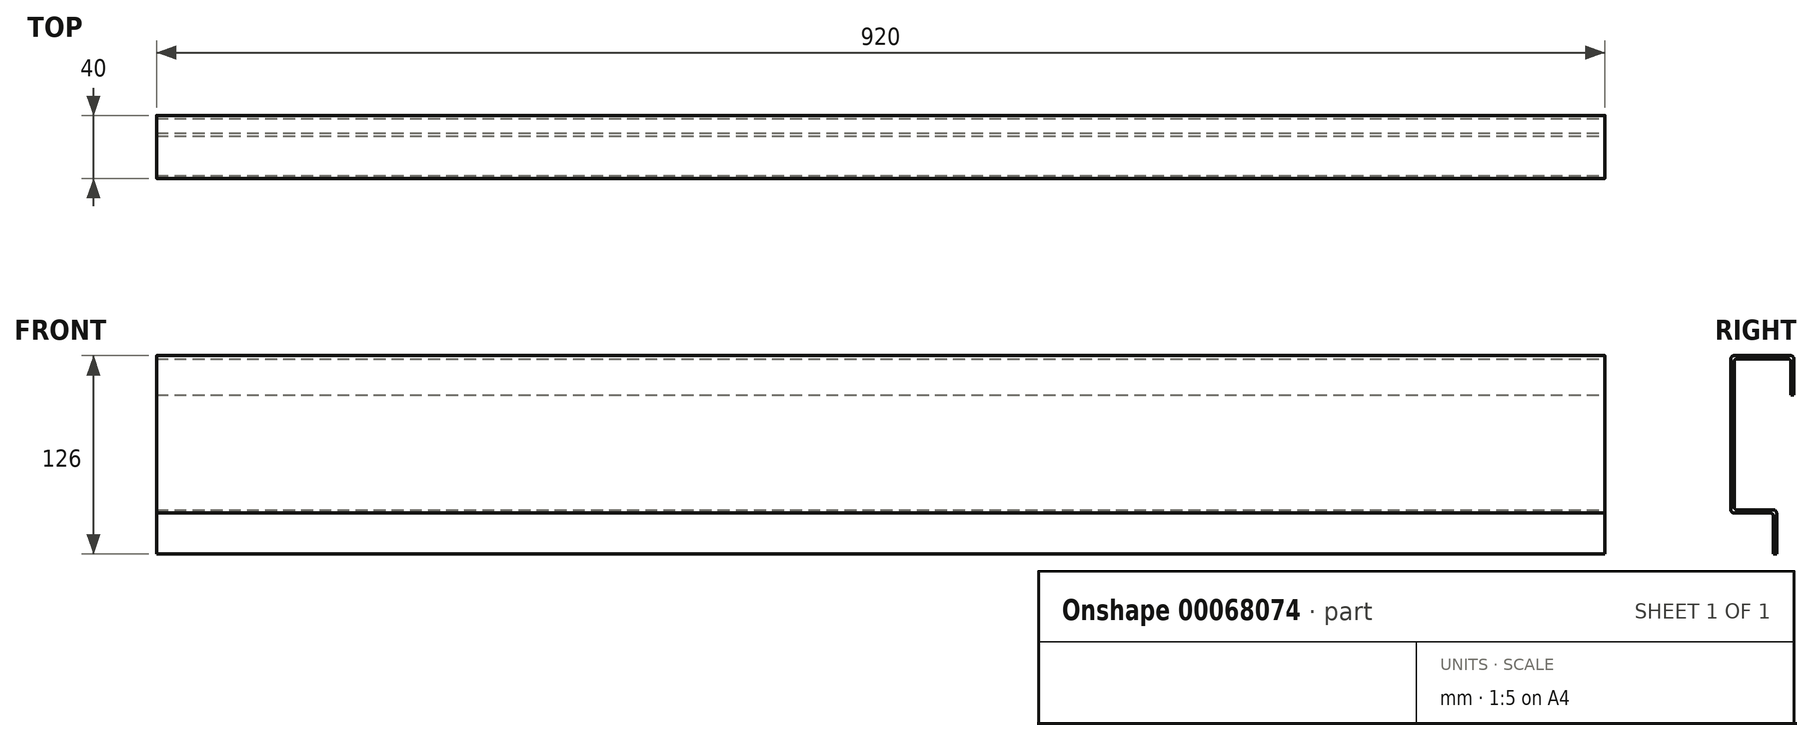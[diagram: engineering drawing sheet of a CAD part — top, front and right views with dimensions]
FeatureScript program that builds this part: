
annotation { "Feature Type Name" : "Feature", "Feature Type Description" : "" }
export const myFeature = defineFeature(function(context is Context, id is Id, definition is map)
    precondition{}
    {
        {
            var Q0;
            Q0=qCreatedBy(makeId("Right.planeOp"),FACE);
            var sketch = newSketch(context, id + "F0", { "sketchPlane" : qUnion([Q0])});
            skLineSegment(sketch, "E0", {"start": v(38, -25) * mm, "end": v(38, -2) * mm});
            skLineSegment(sketch, "E1", {"start": v(38, -2) * mm, "end": v(2, -2) * mm});
            skLineSegment(sketch, "E2", {"start": v(2, -2) * mm, "end": v(2, -98) * mm});
            skLineSegment(sketch, "E3", {"start": v(2, -98) * mm, "end": v(29, -98) * mm});
            skLineSegment(sketch, "E4.0", {"start": v(0, -100) * mm, "end": v(27, -100) * mm});
            skLineSegment(sketch, "E4.1", {"start": v(0, 0) * mm, "end": v(0, -100) * mm});
            skLineSegment(sketch, "E4.2", {"start": v(40, 0) * mm, "end": v(0, 0) * mm});
            skLineSegment(sketch, "E4.3", {"start": v(40, -25) * mm, "end": v(40, 0) * mm});
            skLineSegment(sketch, "E5", {"start": v(29, -98) * mm, "end": v(29, -126) * mm});
            skLineSegment(sketch, "E6", {"start": v(27, -100) * mm, "end": v(27, -126) * mm});
            skLineSegment(sketch, "E7", {"start": v(40, -25) * mm, "end": v(38, -25) * mm});
            skLineSegment(sketch, "E8", {"start": v(29, -126) * mm, "end": v(27, -126) * mm});
            skSolve(sketch);
        }
        {
            var Q0;
            Q0=qCreatedBy(makeId("Top.planeOp"),FACE);
            var sketch = newSketch(context, id + "F1", { "sketchPlane" : qUnion([Q0])});
            skLineSegment(sketch, "E9", {"start": v(0, 0) * mm, "end": v(920, 0) * mm});
            skSolve(sketch);
        }
        {
            var Q0;
            Q0 = qSketchRegion(id + "F0", true);
            var Q1;
            Q1 = qConstructionFilter(qBodyType(qCreatedBy(id + "F1" ,EDGE), BodyType.WIRE), ConstructionObject.NO);
            sweep(context, id + "F2", {"profiles" : qUnion([Q0]), "path" : qUnion([Q1])});
        }
        {
            var Q0;
            Q0=makeQuery(id+"F2.opSweep","SWEPT_EDGE",EDGE,{"disambiguationData":[OSD([sQuery(id+"F0.wireOp",EDGE,"E4.2"),sQuery(id+"F0.wireOp",EDGE,"E4.3"),sQuery(id+"F1.wireOp",EDGE,"E9")])]});
            var Q1;
            Q1=makeQuery(id+"F2.opSweep","SWEPT_EDGE",EDGE,{"disambiguationData":[OSD([sQuery(id+"F0.wireOp",EDGE,"E4.1"),sQuery(id+"F0.wireOp",EDGE,"E4.2"),sQuery(id+"F1.wireOp",EDGE,"E9")])]});
            var Q2;
            Q2=makeQuery(id+"F2.opSweep","SWEPT_EDGE",EDGE,{"disambiguationData":[OSD([sQuery(id+"F0.wireOp",EDGE,"E3"),sQuery(id+"F0.wireOp",EDGE,"E5"),sQuery(id+"F1.wireOp",EDGE,"E9")])]});
            var Q3;
            Q3=makeQuery(id+"F2.opSweep","SWEPT_EDGE",EDGE,{"disambiguationData":[OSD([sQuery(id+"F0.wireOp",EDGE,"E2"),sQuery(id+"F0.wireOp",EDGE,"E3"),sQuery(id+"F1.wireOp",EDGE,"E9")])]});
            var Q4;
            Q4=makeQuery(id+"F2.opSweep","SWEPT_EDGE",EDGE,{"disambiguationData":[OSD([sQuery(id+"F0.wireOp",EDGE,"E1"),sQuery(id+"F0.wireOp",EDGE,"E2"),sQuery(id+"F1.wireOp",EDGE,"E9")])]});
            var Q5;
            Q5=makeQuery(id+"F2.opSweep","SWEPT_EDGE",EDGE,{"disambiguationData":[OSD([sQuery(id+"F0.wireOp",EDGE,"E0"),sQuery(id+"F0.wireOp",EDGE,"E1"),sQuery(id+"F1.wireOp",EDGE,"E9")])]});
            var Q6;
            Q6=makeQuery(id+"F2.opSweep","SWEPT_EDGE",EDGE,{"disambiguationData":[OSD([sQuery(id+"F0.wireOp",EDGE,"E4.0"),sQuery(id+"F0.wireOp",EDGE,"E4.1"),sQuery(id+"F1.wireOp",EDGE,"E9")])]});
            var Q7;
            Q7=makeQuery(id+"F2.opSweep","SWEPT_EDGE",EDGE,{"disambiguationData":[OSD([sQuery(id+"F0.wireOp",EDGE,"E4.0"),sQuery(id+"F0.wireOp",EDGE,"E6"),sQuery(id+"F1.wireOp",EDGE,"E9")])]});
            fillet(context, id + "F3", {"entities" : qUnion([Q0, Q1, Q2, Q3, Q4, Q5, Q6, Q7]), "radius" : 2 * mm, "tangentPropagation" : true, "allowEdgeOverflow" : false});
        }
    });
